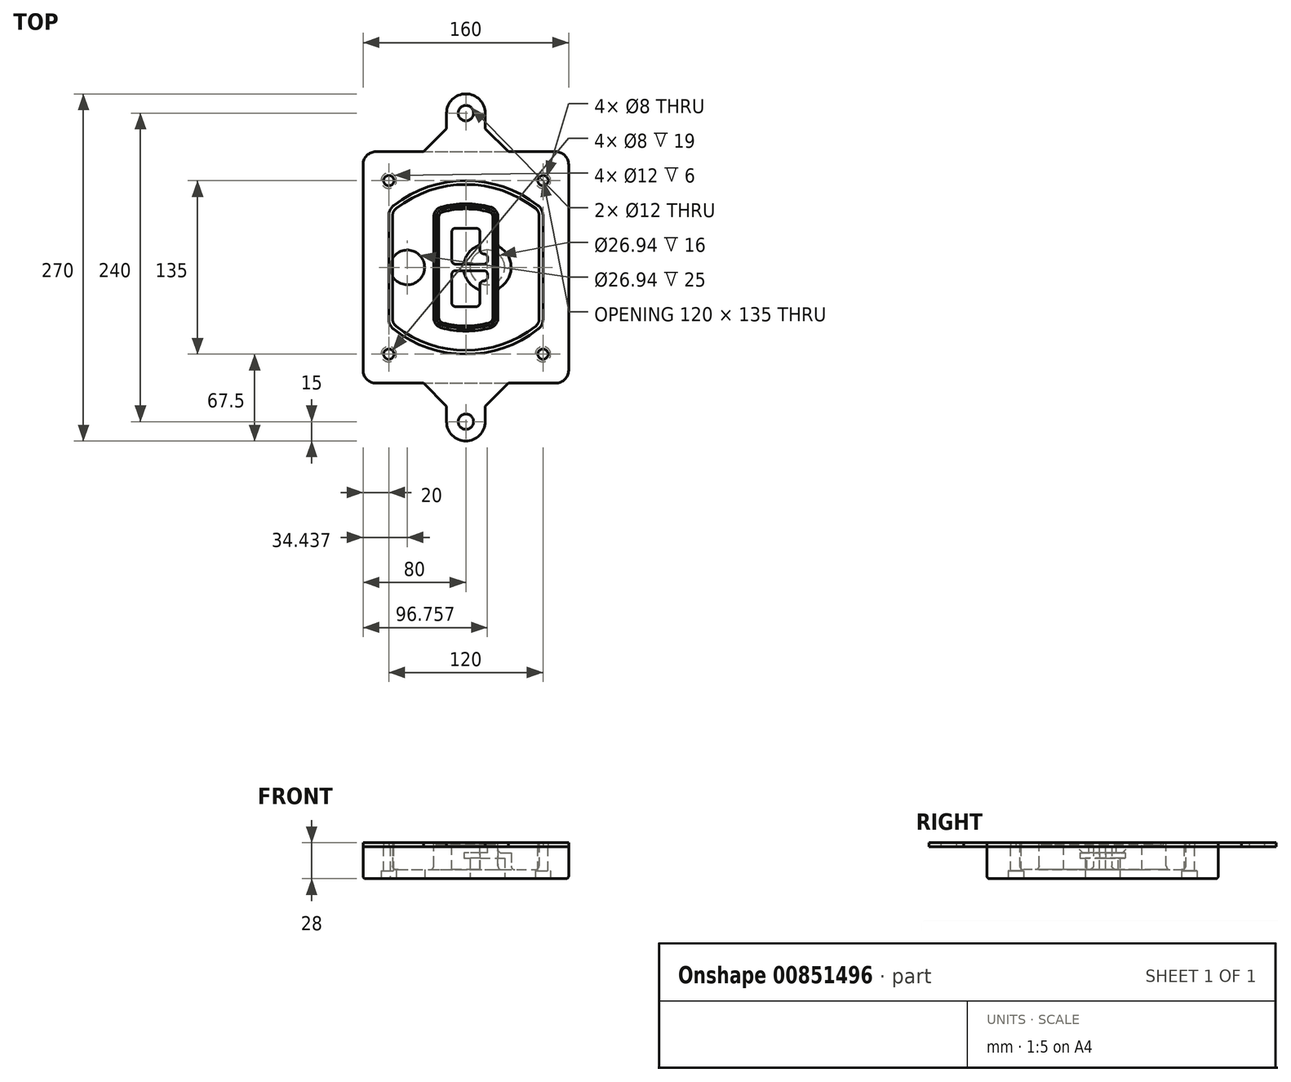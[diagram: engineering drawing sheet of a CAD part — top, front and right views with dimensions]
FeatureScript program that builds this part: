
annotation { "Feature Type Name" : "Feature", "Feature Type Description" : "" }
export const myFeature = defineFeature(function(context is Context, id is Id, definition is map)
    precondition{}
    {
        {
            var Q0;
            Q0=qCreatedBy(makeId("Top.planeOp"),FACE);
            var sketch = newSketch(context, id + "F0", { "sketchPlane" : qUnion([Q0])});
            skPoint(sketch, "E0.rect.middle", {"position": v(0, 0) * mm});
            skLineSegment(sketch, "E1.bottom", {"start": v(-70, -90) * mm, "end": v(70, -90) * mm});
            skLineSegment(sketch, "E1.top", {"start": v(-70, 90) * mm, "end": v(70, 90) * mm});
            skLineSegment(sketch, "E1.left", {"start": v(-80, -80) * mm, "end": v(-80, 80) * mm});
            skLineSegment(sketch, "E1.right", {"start": v(80, -80) * mm, "end": v(80, 80) * mm});
            skLineSegment(sketch, "E2", {"start": v(-80, 90) * mm, "end": v(80, -90) * mm, "construction": true});
            skLineSegment(sketch, "E3", {"start": v(80, 90) * mm, "end": v(-80, -90) * mm, "construction": true});
            skCircle(sketch, "E4", {"center": v(-60, 67.5) * mm, "radius": 4 * mm});
            skCircle(sketch, "E5", {"center": v(60, 67.5) * mm, "radius": 4 * mm});
            skCircle(sketch, "E6", {"center": v(60, -67.5) * mm, "radius": 4 * mm});
            skCircle(sketch, "E7", {"center": v(-60, -67.5) * mm, "radius": 4 * mm});
            skLineSegment(sketch, "E8", {"start": v(-60, 67.5) * mm, "end": v(60, 67.5) * mm, "construction": true});
            skLineSegment(sketch, "E9", {"start": v(60, 67.5) * mm, "end": v(60, -67.5) * mm, "construction": true});
            skLineSegment(sketch, "E10", {"start": v(60, -67.5) * mm, "end": v(-60, -67.5) * mm, "construction": true});
            skLineSegment(sketch, "E11", {"start": v(-60, -67.5) * mm, "end": v(-60, 67.5) * mm, "construction": true});
            skLineSegment(sketch, "E12", {"start": v(-60, 40.3) * mm, "end": v(-60, -40.3) * mm});
            skLineSegment(sketch, "E13", {"start": v(60, 40.3) * mm, "end": v(60, -40.3) * mm});
            skArc(sketch, "E14", {"start": v(56.15, 48.18) * mm, "mid": v(0, 67.5) * mm, "end": v(-56.15, 48.18) * mm});
            skArc(sketch, "E15", {"start": v(-56.15, -48.18) * mm, "mid": v(0, -67.5) * mm, "end": v(56.15, -48.18) * mm});
            skLineSegment(sketch, "E16", {"start": v(-60, 0) * mm, "end": v(60, 0) * mm, "construction": true});
            skPoint(sketch, "E17.visualSharp", {"position": v(-60, -45) * mm});
            skArc(sketch, "E17.filletArc", {"start": v(-60, -40.3) * mm, "mid": v(-58.99, -44.68) * mm, "end": v(-56.15, -48.18) * mm});
            skPoint(sketch, "E18.visualSharp", {"position": v(-60, 45) * mm});
            skArc(sketch, "E18.filletArc", {"start": v(-56.15, 48.18) * mm, "mid": v(-58.99, 44.68) * mm, "end": v(-60, 40.3) * mm});
            skPoint(sketch, "E19.visualSharp", {"position": v(60, 45) * mm});
            skArc(sketch, "E19.filletArc", {"start": v(60, 40.3) * mm, "mid": v(58.99, 44.68) * mm, "end": v(56.15, 48.18) * mm});
            skPoint(sketch, "E20.visualSharp", {"position": v(60, -45) * mm});
            skArc(sketch, "E20.filletArc", {"start": v(56.15, -48.18) * mm, "mid": v(58.99, -44.68) * mm, "end": v(60, -40.3) * mm});
            skPoint(sketch, "E21.visualSharp", {"position": v(-80, 90) * mm});
            skArc(sketch, "E21.filletArc", {"start": v(-70, 90) * mm, "mid": v(-77.07, 87.07) * mm, "end": v(-80, 80) * mm});
            skPoint(sketch, "E22.visualSharp", {"position": v(80, 90) * mm});
            skArc(sketch, "E22.filletArc", {"start": v(80, 80) * mm, "mid": v(77.07, 87.07) * mm, "end": v(70, 90) * mm});
            skPoint(sketch, "E23.visualSharp", {"position": v(80, -90) * mm});
            skArc(sketch, "E23.filletArc", {"start": v(70, -90) * mm, "mid": v(77.07, -87.07) * mm, "end": v(80, -80) * mm});
            skPoint(sketch, "E24.visualSharp", {"position": v(-80, -90) * mm});
            skArc(sketch, "E24.filletArc", {"start": v(-80, -80) * mm, "mid": v(-77.07, -87.07) * mm, "end": v(-70, -90) * mm});
            skArc(sketch, "E25.0", {"start": v(57, 40.3) * mm, "mid": v(56.3, 43.36) * mm, "end": v(54.3, 45.81) * mm});
            skLineSegment(sketch, "E25.1", {"start": v(57, 40.3) * mm, "end": v(57, -40.3) * mm});
            skArc(sketch, "E25.2", {"start": v(54.3, -45.81) * mm, "mid": v(56.3, -43.36) * mm, "end": v(57, -40.3) * mm});
            skArc(sketch, "E25.3", {"start": v(-54.3, -45.81) * mm, "mid": v(0, -64.5) * mm, "end": v(54.3, -45.81) * mm});
            skArc(sketch, "E25.4", {"start": v(-57, -40.3) * mm, "mid": v(-56.3, -43.36) * mm, "end": v(-54.3, -45.81) * mm});
            skArc(sketch, "E25.5", {"start": v(54.3, 45.81) * mm, "mid": v(0, 64.5) * mm, "end": v(-54.3, 45.81) * mm});
            skLineSegment(sketch, "E25.6", {"start": v(-57, 40.3) * mm, "end": v(-57, -40.3) * mm});
            skArc(sketch, "E25.7", {"start": v(-54.3, 45.81) * mm, "mid": v(-56.3, 43.36) * mm, "end": v(-57, 40.3) * mm});
            skArc(sketch, "E26.0", {"start": v(-58.62, 51.33) * mm, "mid": v(-62.58, 46.43) * mm, "end": v(-64, 40.3) * mm});
            skArc(sketch, "E26.1", {"start": v(58.62, 51.33) * mm, "mid": v(0, 71.5) * mm, "end": v(-58.62, 51.33) * mm});
            skArc(sketch, "E26.2", {"start": v(64, 40.3) * mm, "mid": v(62.58, 46.43) * mm, "end": v(58.62, 51.33) * mm});
            skLineSegment(sketch, "E26.3", {"start": v(64, 40.3) * mm, "end": v(64, -40.3) * mm});
            skArc(sketch, "E26.4", {"start": v(58.62, -51.33) * mm, "mid": v(62.58, -46.43) * mm, "end": v(64, -40.3) * mm});
            skLineSegment(sketch, "E26.5", {"start": v(-64, 40.3) * mm, "end": v(-64, -40.3) * mm});
            skArc(sketch, "E26.6", {"start": v(-58.62, -51.33) * mm, "mid": v(0, -71.5) * mm, "end": v(58.62, -51.33) * mm});
            skArc(sketch, "E26.7", {"start": v(-64, -40.3) * mm, "mid": v(-62.58, -46.43) * mm, "end": v(-58.62, -51.33) * mm});
            skSolve(sketch);
        }
        {
            var Q0;
            Q0=makeQuery(id+"F0.imprint","IMPRINT",FACE,{"disambiguationData":[TD([[makeQuery(id+"F0.imprint","IMPRINT",EDGE,{"derivedFrom":sQuery(id+"F0.wireOp",EDGE,"E1.bottom")}),1.0]])]});
            var Q1;
            Q1=makeQuery(id+"F0.imprint","IMPRINT",FACE,{"disambiguationData":[TD([[makeQuery(id+"F0.imprint","IMPRINT",EDGE,{"derivedFrom":sQuery(id+"F0.wireOp",EDGE,"E12")}),1.0]])]});
            var Q2;
            Q2=makeQuery(id+"F0.imprint","IMPRINT",FACE,{"disambiguationData":[TD([[makeQuery(id+"F0.imprint","IMPRINT",EDGE,{"derivedFrom":sQuery(id+"F0.wireOp",EDGE,"E25.0")}),1.0]])]});
            var Q3;
            Q3=makeQuery(id+"F0.imprint","IMPRINT",FACE,{"disambiguationData":[TD([[makeQuery(id+"F0.imprint","IMPRINT",EDGE,{"derivedFrom":sQuery(id+"F0.wireOp",EDGE,"E12")}),-1.0]])]});
            extrude(context, id + "F1", {"entities" : qUnion([Q0, Q1, Q2, Q3]), "oppositeDirection" : true, "depth" : 25 * mm});
        }
        {
            var Q0;
            Q0=makeQuery(id+"F0.imprint","IMPRINT",FACE,{"disambiguationData":[TD([[makeQuery(id+"F0.imprint","IMPRINT",EDGE,{"derivedFrom":sQuery(id+"F0.wireOp",EDGE,"E12")}),1.0]])]});
            extrude(context, id + "F2", {"entities" : qUnion([Q0]), "operationType" : NewBodyOperationType.ADD, "depth" : 3 * mm});
        }
        {
            var Q0;
            Q0=makeQuery(id+"F0.imprint","IMPRINT",FACE,{"disambiguationData":[TD([[makeQuery(id+"F0.imprint","IMPRINT",EDGE,{"derivedFrom":sQuery(id+"F0.wireOp",EDGE,"E25.0")}),1.0]])]});
            extrude(context, id + "F3", {"entities" : qUnion([Q0]), "operationType" : NewBodyOperationType.REMOVE, "oppositeDirection" : true, "depth" : 18 * mm});
        }
        {
            var Q0;
            Q0=makeQuery(id+"F2.opExtrude","CAP_FACE",FACE,{"disambiguationData":[OSD([sQuery(id+"F0.wireOp",EDGE,"E12"),sQuery(id+"F0.wireOp",EDGE,"E13"),sQuery(id+"F0.wireOp",EDGE,"E14"),sQuery(id+"F0.wireOp",EDGE,"E15"),sQuery(id+"F0.wireOp",EDGE,"E17.filletArc"),sQuery(id+"F0.wireOp",EDGE,"E18.filletArc"),sQuery(id+"F0.wireOp",EDGE,"E19.filletArc"),sQuery(id+"F0.wireOp",EDGE,"E20.filletArc"),sQuery(id+"F0.wireOp",EDGE,"E25.0"),sQuery(id+"F0.wireOp",EDGE,"E25.1"),sQuery(id+"F0.wireOp",EDGE,"E25.2"),sQuery(id+"F0.wireOp",EDGE,"E25.3"),sQuery(id+"F0.wireOp",EDGE,"E25.4"),sQuery(id+"F0.wireOp",EDGE,"E25.5"),sQuery(id+"F0.wireOp",EDGE,"E25.6"),sQuery(id+"F0.wireOp",EDGE,"E25.7")])],"isStart":false});
            var sketch = newSketch(context, id + "F4", { "sketchPlane" : qUnion([Q0])});
            skArc(sketch, "E27.0", {"start": v(-19.08, -46.97) * mm, "mid": v(0, -49.5) * mm, "end": v(19.08, -46.97) * mm});
            skArc(sketch, "E28.0", {"start": v(19.08, 46.97) * mm, "mid": v(0, 49.5) * mm, "end": v(-19.08, 46.97) * mm});
            skLineSegment(sketch, "E29", {"start": v(-25, 39.25) * mm, "end": v(-25, -39.25) * mm});
            skLineSegment(sketch, "E30", {"start": v(25, 39.25) * mm, "end": v(25, -39.25) * mm});
            skLineSegment(sketch, "E31", {"start": v(-25, 45.1) * mm, "end": v(25, 45.1) * mm, "construction": true});
            skLineSegment(sketch, "E32", {"start": v(-25, -45.1) * mm, "end": v(25, -45.1) * mm, "construction": true});
            skPoint(sketch, "E33.visualSharp", {"position": v(-25, 45.1) * mm});
            skArc(sketch, "E33.filletArc", {"start": v(-19.08, 46.97) * mm, "mid": v(-23.35, 44.11) * mm, "end": v(-25, 39.25) * mm});
            skPoint(sketch, "E34.visualSharp", {"position": v(25, 45.1) * mm});
            skArc(sketch, "E34.filletArc", {"start": v(25, 39.25) * mm, "mid": v(23.35, 44.11) * mm, "end": v(19.08, 46.97) * mm});
            skPoint(sketch, "E35.visualSharp", {"position": v(25, -45.1) * mm});
            skArc(sketch, "E35.filletArc", {"start": v(19.08, -46.97) * mm, "mid": v(23.35, -44.11) * mm, "end": v(25, -39.25) * mm});
            skPoint(sketch, "E36.visualSharp", {"position": v(-25, -45.1) * mm});
            skArc(sketch, "E36.filletArc", {"start": v(-25, -39.25) * mm, "mid": v(-23.35, -44.11) * mm, "end": v(-19.08, -46.97) * mm});
            skArc(sketch, "E37.0", {"start": v(54.3, 45.81) * mm, "mid": v(0, 64.5) * mm, "end": v(-54.3, 45.81) * mm});
            skArc(sketch, "E37.1", {"start": v(-54.3, 45.81) * mm, "mid": v(-56.3, 43.36) * mm, "end": v(-57, 40.3) * mm});
            skLineSegment(sketch, "E37.2", {"start": v(-57, 40.3) * mm, "end": v(-57, -40.3) * mm});
            skArc(sketch, "E37.3", {"start": v(-57, -40.3) * mm, "mid": v(-56.3, -43.36) * mm, "end": v(-54.3, -45.81) * mm});
            skArc(sketch, "E37.4", {"start": v(-54.3, -45.81) * mm, "mid": v(0, -64.5) * mm, "end": v(54.3, -45.81) * mm});
            skArc(sketch, "E37.5", {"start": v(54.3, -45.81) * mm, "mid": v(56.3, -43.36) * mm, "end": v(57, -40.3) * mm});
            skLineSegment(sketch, "E37.6", {"start": v(57, 40.3) * mm, "end": v(57, -40.3) * mm});
            skArc(sketch, "E37.7", {"start": v(57, 40.3) * mm, "mid": v(56.3, 43.36) * mm, "end": v(54.3, 45.81) * mm});
            skLineSegment(sketch, "E38.0", {"start": v(23, 39.25) * mm, "end": v(23, -39.25) * mm});
            skArc(sketch, "E38.1", {"start": v(18.56, -45.04) * mm, "mid": v(21.76, -42.9) * mm, "end": v(23, -39.25) * mm});
            skArc(sketch, "E38.2", {"start": v(-18.56, -45.04) * mm, "mid": v(0, -47.5) * mm, "end": v(18.56, -45.04) * mm});
            skArc(sketch, "E38.3", {"start": v(-23, -39.25) * mm, "mid": v(-21.76, -42.9) * mm, "end": v(-18.56, -45.04) * mm});
            skLineSegment(sketch, "E38.4", {"start": v(-23, 39.25) * mm, "end": v(-23, -39.25) * mm});
            skArc(sketch, "E38.5", {"start": v(23, 39.25) * mm, "mid": v(21.76, 42.9) * mm, "end": v(18.56, 45.04) * mm});
            skArc(sketch, "E38.6", {"start": v(-18.56, 45.04) * mm, "mid": v(-21.76, 42.9) * mm, "end": v(-23, 39.25) * mm});
            skArc(sketch, "E38.7", {"start": v(18.56, 45.04) * mm, "mid": v(0, 47.5) * mm, "end": v(-18.56, 45.04) * mm});
            skArc(sketch, "E39.0", {"start": v(21, 39.25) * mm, "mid": v(20.18, 41.68) * mm, "end": v(18.04, 43.1) * mm});
            skLineSegment(sketch, "E39.1", {"start": v(21, 39.25) * mm, "end": v(21, -39.25) * mm});
            skArc(sketch, "E39.2", {"start": v(18.04, -43.1) * mm, "mid": v(20.18, -41.68) * mm, "end": v(21, -39.25) * mm});
            skArc(sketch, "E39.3", {"start": v(-18.04, -43.1) * mm, "mid": v(0, -45.5) * mm, "end": v(18.04, -43.1) * mm});
            skArc(sketch, "E39.4", {"start": v(-21, -39.25) * mm, "mid": v(-20.18, -41.68) * mm, "end": v(-18.04, -43.1) * mm});
            skArc(sketch, "E39.5", {"start": v(18.04, 43.1) * mm, "mid": v(0, 45.5) * mm, "end": v(-18.04, 43.1) * mm});
            skLineSegment(sketch, "E39.6", {"start": v(-21, 39.25) * mm, "end": v(-21, -39.25) * mm});
            skArc(sketch, "E39.7", {"start": v(-18.04, 43.1) * mm, "mid": v(-20.18, 41.68) * mm, "end": v(-21, 39.25) * mm});
            skLineSegment(sketch, "E40", {"start": v(-25, 0) * mm, "end": v(25, 0) * mm, "construction": true});
            skLineSegment(sketch, "E41", {"start": v(-11, 5.5) * mm, "end": v(-11, 27.5) * mm});
            skLineSegment(sketch, "E42", {"start": v(-8, 30.5) * mm, "end": v(8, 30.5) * mm});
            skLineSegment(sketch, "E43", {"start": v(11, 27.5) * mm, "end": v(11, 13.5) * mm});
            skLineSegment(sketch, "E44", {"start": v(14, 10.5) * mm, "end": v(14, 10.5) * mm});
            skLineSegment(sketch, "E45", {"start": v(17, 7.5) * mm, "end": v(17, 5.5) * mm});
            skLineSegment(sketch, "E46", {"start": v(14, 2.5) * mm, "end": v(-8, 2.5) * mm});
            skPoint(sketch, "E47.visualSharp", {"position": v(-11, 30.5) * mm});
            skArc(sketch, "E47.filletArc", {"start": v(-8, 30.5) * mm, "mid": v(-10.12, 29.62) * mm, "end": v(-11, 27.5) * mm});
            skPoint(sketch, "E48.visualSharp", {"position": v(11, 30.5) * mm});
            skArc(sketch, "E48.filletArc", {"start": v(11, 27.5) * mm, "mid": v(10.12, 29.62) * mm, "end": v(8, 30.5) * mm});
            skPoint(sketch, "E49.visualSharp", {"position": v(11, 10.5) * mm});
            skArc(sketch, "E49.filletArc", {"start": v(11, 13.5) * mm, "mid": v(11.88, 11.38) * mm, "end": v(14, 10.5) * mm});
            skPoint(sketch, "E50.visualSharp", {"position": v(17, 10.5) * mm});
            skArc(sketch, "E50.filletArc", {"start": v(17, 7.5) * mm, "mid": v(16.12, 9.62) * mm, "end": v(14, 10.5) * mm});
            skPoint(sketch, "E51.visualSharp", {"position": v(17, 2.5) * mm});
            skArc(sketch, "E51.filletArc", {"start": v(14, 2.5) * mm, "mid": v(16.12, 3.38) * mm, "end": v(17, 5.5) * mm});
            skPoint(sketch, "E52.visualSharp", {"position": v(-11, 2.5) * mm});
            skArc(sketch, "E52.filletArc", {"start": v(-11, 5.5) * mm, "mid": v(-10.12, 3.38) * mm, "end": v(-8, 2.5) * mm});
            skLineSegment(sketch, "E53.0.MirrorCS", {"start": v(14, -2.5) * mm, "end": v(-8, -2.5) * mm});
            skArc(sketch, "E54.0.MirrorCS", {"start": v(-11, -5.5) * mm, "mid": v(-10.12, -3.38) * mm, "end": v(-8, -2.5) * mm});
            skLineSegment(sketch, "E55.0.MirrorCS", {"start": v(-11, -5.5) * mm, "end": v(-11, -27.5) * mm});
            skArc(sketch, "E56.0.MirrorCS", {"start": v(-8, -30.5) * mm, "mid": v(-10.12, -29.62) * mm, "end": v(-11, -27.5) * mm});
            skLineSegment(sketch, "E57.0.MirrorCS", {"start": v(-8, -30.5) * mm, "end": v(8, -30.5) * mm});
            skArc(sketch, "E58.0.MirrorCS", {"start": v(11, -27.5) * mm, "mid": v(10.12, -29.62) * mm, "end": v(8, -30.5) * mm});
            skLineSegment(sketch, "E59.0.MirrorCS", {"start": v(11, -27.5) * mm, "end": v(11, -13.5) * mm});
            skArc(sketch, "E60.0.MirrorCS", {"start": v(11, -13.5) * mm, "mid": v(11.88, -11.38) * mm, "end": v(14, -10.5) * mm});
            skArc(sketch, "E61.0.MirrorCS", {"start": v(17, -7.5) * mm, "mid": v(16.12, -9.62) * mm, "end": v(14, -10.5) * mm});
            skLineSegment(sketch, "E62.0.MirrorCS", {"start": v(17, -7.5) * mm, "end": v(17, -5.5) * mm});
            skArc(sketch, "E63.0.MirrorCS", {"start": v(14, -2.5) * mm, "mid": v(16.12, -3.38) * mm, "end": v(17, -5.5) * mm});
            skSolve(sketch);
        }
        {
            var Q0;
            Q0=makeQuery(id+"F4.imprint","IMPRINT",FACE,{"disambiguationData":[TD([[makeQuery(id+"F4.imprint","IMPRINT",EDGE,{"derivedFrom":sQuery(id+"F4.wireOp",EDGE,"E27.0")}),1.0]])]});
            var Q1;
            Q1=makeQuery(id+"F4.imprint","IMPRINT",FACE,{"disambiguationData":[TD([[makeQuery(id+"F4.imprint","IMPRINT",EDGE,{"derivedFrom":sQuery(id+"F4.wireOp",EDGE,"E38.0")}),-1.0]])]});
            var Q2;
            Q2=makeQuery(id+"F4.imprint","IMPRINT",FACE,{"disambiguationData":[TD([[makeQuery(id+"F4.imprint","IMPRINT",EDGE,{"derivedFrom":sQuery(id+"F4.wireOp",EDGE,"E39.0")}),1.0]])]});
            extrude(context, id + "F5", {"entities" : qUnion([Q0, Q1, Q2]), "operationType" : NewBodyOperationType.ADD, "endBound" : BoundingType.UP_TO_NEXT, "oppositeDirection" : true, "depth" : 25 * mm});
        }
        {
            var Q0;
            Q0=makeQuery(id+"F4.imprint","IMPRINT",FACE,{"disambiguationData":[TD([[makeQuery(id+"F4.imprint","IMPRINT",EDGE,{"derivedFrom":sQuery(id+"F4.wireOp",EDGE,"E38.0")}),-1.0]])]});
            extrude(context, id + "F6", {"entities" : qUnion([Q0]), "operationType" : NewBodyOperationType.REMOVE, "oppositeDirection" : true, "depth" : 2 * mm});
        }
        {
            var Q0;
            Q0=makeQuery(id+"F1.opExtrude","CAP_FACE",FACE,{"disambiguationData":[OSD([sQuery(id+"F0.wireOp",EDGE,"E1.bottom"),sQuery(id+"F0.wireOp",EDGE,"E1.top"),sQuery(id+"F0.wireOp",EDGE,"E1.left"),sQuery(id+"F0.wireOp",EDGE,"E1.right"),sQuery(id+"F0.wireOp",EDGE,"E4"),sQuery(id+"F0.wireOp",EDGE,"E5"),sQuery(id+"F0.wireOp",EDGE,"E6"),sQuery(id+"F0.wireOp",EDGE,"E7"),sQuery(id+"F0.wireOp",EDGE,"E21.filletArc"),sQuery(id+"F0.wireOp",EDGE,"E22.filletArc"),sQuery(id+"F0.wireOp",EDGE,"E23.filletArc"),sQuery(id+"F0.wireOp",EDGE,"E24.filletArc")])],"isStart":false});
            var sketch = newSketch(context, id + "F7", { "sketchPlane" : qUnion([Q0])});
            skCircle(sketch, "E64", {"center": v(16.76, 0) * mm, "radius": 13.47 * mm});
            skCircle(sketch, "E65", {"center": v(-45.56, 0) * mm, "radius": 13.47 * mm});
            skLineSegment(sketch, "E66", {"start": v(80, 0) * mm, "end": v(-80, 0) * mm});
            skCircle(sketch, "E67", {"center": v(16.76, 0) * mm, "radius": 18.47 * mm});
            skCircle(sketch, "E68", {"center": v(60, -67.5) * mm, "radius": 6 * mm});
            skCircle(sketch, "E69", {"center": v(-60, -67.5) * mm, "radius": 6 * mm});
            skCircle(sketch, "E70", {"center": v(-60, 67.5) * mm, "radius": 6 * mm});
            skCircle(sketch, "E71", {"center": v(60, 67.5) * mm, "radius": 6 * mm});
            skSolve(sketch);
        }
        {
            var Q0;
            {var subQ1=sQuery(id+"F7.wireOp",EDGE,"E66");var subQ4=sQuery(id+"F7.wireOp",EDGE,"E64");var subQ6=makeQuery(id+"F7.imprint","INTERSECT",VERTEX,{"disambiguationData":[OD(0.0)],"derivedFrom":[subQ4,subQ1]});Q0=makeQuery(id+"F7.imprint","IMPRINT",FACE,{"disambiguationData":[TD([[makeQuery(id+"F7.imprint","IMPRINT",EDGE,{"disambiguationData":[TD([[subQ6,-1.0]])],"derivedFrom":subQ4}),-1.0]])]});}
            var Q1;
            {var subQ0=sQuery(id+"F7.wireOp",EDGE,"E66");var subQ1=sQuery(id+"F7.wireOp",EDGE,"E64");var subQ3=makeQuery(id+"F7.imprint","INTERSECT",VERTEX,{"disambiguationData":[OD(0.0)],"derivedFrom":[subQ1,subQ0]});Q1=makeQuery(id+"F7.imprint","IMPRINT",FACE,{"disambiguationData":[TD([[makeQuery(id+"F7.imprint","IMPRINT",EDGE,{"disambiguationData":[TD([[subQ3,-1.0]])],"derivedFrom":subQ1}),1.0]])]});}
            var Q2;
            {var subQ0=sQuery(id+"F7.wireOp",EDGE,"E66");var subQ1=sQuery(id+"F7.wireOp",EDGE,"E64");var subQ3=makeQuery(id+"F7.imprint","INTERSECT",VERTEX,{"disambiguationData":[OD(0.0)],"derivedFrom":[subQ1,subQ0]});Q2=makeQuery(id+"F7.imprint","IMPRINT",FACE,{"disambiguationData":[TD([[makeQuery(id+"F7.imprint","IMPRINT",EDGE,{"disambiguationData":[TD([[subQ3,1.0]])],"derivedFrom":subQ1}),1.0]])]});}
            var Q3;
            {var subQ1=sQuery(id+"F7.wireOp",EDGE,"E66");var subQ4=sQuery(id+"F7.wireOp",EDGE,"E64");var subQ6=makeQuery(id+"F7.imprint","INTERSECT",VERTEX,{"disambiguationData":[OD(0.0)],"derivedFrom":[subQ4,subQ1]});Q3=makeQuery(id+"F7.imprint","IMPRINT",FACE,{"disambiguationData":[TD([[makeQuery(id+"F7.imprint","IMPRINT",EDGE,{"disambiguationData":[TD([[subQ6,1.0]])],"derivedFrom":subQ4}),-1.0]])]});}
            extrude(context, id + "F8", {"entities" : qUnion([Q0, Q1, Q2, Q3]), "operationType" : NewBodyOperationType.ADD, "oppositeDirection" : true, "depth" : 20 * mm});
        }
        {
            var Q0;
            {var subQ0=sQuery(id+"F7.wireOp",EDGE,"E66");var subQ1=sQuery(id+"F7.wireOp",EDGE,"E64");var subQ3=makeQuery(id+"F7.imprint","INTERSECT",VERTEX,{"disambiguationData":[OD(0.0)],"derivedFrom":[subQ1,subQ0]});Q0=makeQuery(id+"F7.imprint","IMPRINT",FACE,{"disambiguationData":[TD([[makeQuery(id+"F7.imprint","IMPRINT",EDGE,{"disambiguationData":[TD([[subQ3,-1.0]])],"derivedFrom":subQ1}),1.0]])]});}
            var Q1;
            {var subQ0=sQuery(id+"F7.wireOp",EDGE,"E66");var subQ1=sQuery(id+"F7.wireOp",EDGE,"E64");var subQ3=makeQuery(id+"F7.imprint","INTERSECT",VERTEX,{"disambiguationData":[OD(0.0)],"derivedFrom":[subQ1,subQ0]});Q1=makeQuery(id+"F7.imprint","IMPRINT",FACE,{"disambiguationData":[TD([[makeQuery(id+"F7.imprint","IMPRINT",EDGE,{"disambiguationData":[TD([[subQ3,1.0]])],"derivedFrom":subQ1}),1.0]])]});}
            extrude(context, id + "F9", {"entities" : qUnion([Q0, Q1]), "operationType" : NewBodyOperationType.REMOVE, "oppositeDirection" : true, "depth" : 16 * mm});
        }
        {
            var Q0;
            {var subQ0=sQuery(id+"F7.wireOp",EDGE,"E66");var subQ1=sQuery(id+"F7.wireOp",EDGE,"E65");var subQ3=makeQuery(id+"F7.imprint","INTERSECT",VERTEX,{"disambiguationData":[OD(0.0)],"derivedFrom":[subQ1,subQ0]});Q0=makeQuery(id+"F7.imprint","IMPRINT",FACE,{"disambiguationData":[TD([[makeQuery(id+"F7.imprint","IMPRINT",EDGE,{"disambiguationData":[TD([[subQ3,-1.0]])],"derivedFrom":subQ1}),1.0]])]});}
            var Q1;
            {var subQ0=sQuery(id+"F7.wireOp",EDGE,"E66");var subQ1=sQuery(id+"F7.wireOp",EDGE,"E65");var subQ3=makeQuery(id+"F7.imprint","INTERSECT",VERTEX,{"disambiguationData":[OD(0.0)],"derivedFrom":[subQ1,subQ0]});Q1=makeQuery(id+"F7.imprint","IMPRINT",FACE,{"disambiguationData":[TD([[makeQuery(id+"F7.imprint","IMPRINT",EDGE,{"disambiguationData":[TD([[subQ3,1.0]])],"derivedFrom":subQ1}),1.0]])]});}
            extrude(context, id + "F10", {"entities" : qUnion([Q0, Q1]), "operationType" : NewBodyOperationType.REMOVE, "oppositeDirection" : true, "depth" : 25 * mm});
        }
        {
            var Q0;
            Q0=makeQuery(id+"F7.imprint","IMPRINT",FACE,{"disambiguationData":[TD([[makeQuery(id+"F7.imprint","IMPRINT",EDGE,{"derivedFrom":sQuery(id+"F7.wireOp",EDGE,"E68")}),1.0]])]});
            var Q1;
            Q1=makeQuery(id+"F7.imprint","IMPRINT",FACE,{"disambiguationData":[TD([[makeQuery(id+"F7.imprint","IMPRINT",EDGE,{"derivedFrom":makeQuery(id+"F1.opExtrude","CAP_EDGE",EDGE,{"disambiguationData":[OSD([sQuery(id+"F0.wireOp",EDGE,"E5")])],"isStart":false})}),-1.0]])]});
            var Q2;
            Q2=makeQuery(id+"F7.imprint","IMPRINT",FACE,{"disambiguationData":[TD([[makeQuery(id+"F7.imprint","IMPRINT",EDGE,{"derivedFrom":sQuery(id+"F7.wireOp",EDGE,"E69")}),1.0]])]});
            var Q3;
            Q3=makeQuery(id+"F7.imprint","IMPRINT",FACE,{"disambiguationData":[TD([[makeQuery(id+"F7.imprint","IMPRINT",EDGE,{"derivedFrom":makeQuery(id+"F1.opExtrude","CAP_EDGE",EDGE,{"disambiguationData":[OSD([sQuery(id+"F0.wireOp",EDGE,"E4")])],"isStart":false})}),-1.0]])]});
            var Q4;
            Q4=makeQuery(id+"F7.imprint","IMPRINT",FACE,{"disambiguationData":[TD([[makeQuery(id+"F7.imprint","IMPRINT",EDGE,{"derivedFrom":sQuery(id+"F7.wireOp",EDGE,"E70")}),1.0]])]});
            var Q5;
            Q5=makeQuery(id+"F7.imprint","IMPRINT",FACE,{"disambiguationData":[TD([[makeQuery(id+"F7.imprint","IMPRINT",EDGE,{"derivedFrom":makeQuery(id+"F1.opExtrude","CAP_EDGE",EDGE,{"disambiguationData":[OSD([sQuery(id+"F0.wireOp",EDGE,"E7")])],"isStart":false})}),-1.0]])]});
            var Q6;
            Q6=makeQuery(id+"F7.imprint","IMPRINT",FACE,{"disambiguationData":[TD([[makeQuery(id+"F7.imprint","IMPRINT",EDGE,{"derivedFrom":sQuery(id+"F7.wireOp",EDGE,"E71")}),1.0]])]});
            var Q7;
            Q7=makeQuery(id+"F7.imprint","IMPRINT",FACE,{"disambiguationData":[TD([[makeQuery(id+"F7.imprint","IMPRINT",EDGE,{"derivedFrom":makeQuery(id+"F1.opExtrude","CAP_EDGE",EDGE,{"disambiguationData":[OSD([sQuery(id+"F0.wireOp",EDGE,"E6")])],"isStart":false})}),-1.0]])]});
            extrude(context, id + "F11", {"entities" : qUnion([Q0, Q1, Q2, Q3, Q4, Q5, Q6, Q7]), "operationType" : NewBodyOperationType.REMOVE, "oppositeDirection" : true, "depth" : 6 * mm});
        }
        {
            var Q0;
            Q0=makeQuery(id+"F9.boolean.opBoolean","COPY",FACE,{"derivedFrom":makeQuery(id+"F9.opExtrude","CAP_FACE",FACE,{"disambiguationData":[OSD([sQuery(id+"F7.wireOp",EDGE,"E64")])],"isStart":false})});
            var sketch = newSketch(context, id + "F12", { "sketchPlane" : qUnion([Q0])});
            skArc(sketch, "E72.0", {"start": v(11, 17.55) * mm, "mid": v(2.57, 11.82) * mm, "end": v(-1.54, 2.5) * mm});
            skArc(sketch, "E72.1", {"start": v(-1.54, -2.5) * mm, "mid": v(2.57, -11.82) * mm, "end": v(11, -17.55) * mm});
            skLineSegment(sketch, "E73", {"start": v(-1.54, -2.5) * mm, "end": v(14, -2.5) * mm});
            skLineSegment(sketch, "E74.0", {"start": v(14, 2.5) * mm, "end": v(-1.54, 2.5) * mm});
            skArc(sketch, "E74.1", {"start": v(14, 2.5) * mm, "mid": v(16.12, 3.38) * mm, "end": v(17, 5.5) * mm});
            skLineSegment(sketch, "E74.2", {"start": v(17, 7.5) * mm, "end": v(17, 5.5) * mm});
            skArc(sketch, "E74.3", {"start": v(17, 7.5) * mm, "mid": v(16.12, 9.62) * mm, "end": v(14, 10.5) * mm});
            skArc(sketch, "E74.4", {"start": v(11, 13.5) * mm, "mid": v(11.88, 11.38) * mm, "end": v(14, 10.5) * mm});
            skLineSegment(sketch, "E74.5", {"start": v(11, 17.55) * mm, "end": v(11, 13.5) * mm});
            skLineSegment(sketch, "E74.7", {"start": v(14, -2.5) * mm, "end": v(-1.54, -2.5) * mm});
            skArc(sketch, "E74.8", {"start": v(14, -2.5) * mm, "mid": v(16.12, -3.38) * mm, "end": v(17, -5.5) * mm});
            skLineSegment(sketch, "E74.9", {"start": v(17, -7.5) * mm, "end": v(17, -5.5) * mm});
            skArc(sketch, "E74.10", {"start": v(17, -7.5) * mm, "mid": v(16.12, -9.62) * mm, "end": v(14, -10.5) * mm});
            skArc(sketch, "E74.11", {"start": v(11, -13.5) * mm, "mid": v(11.88, -11.38) * mm, "end": v(14, -10.5) * mm});
            skLineSegment(sketch, "E74.12", {"start": v(11, -17.55) * mm, "end": v(11, -13.5) * mm});
            skPoint(sketch, "E75.orphan", {"position": v(11, -27.5) * mm});
            skPoint(sketch, "E76.orphan", {"position": v(-8, -2.5) * mm});
            skPoint(sketch, "E77.orphan", {"position": v(-8, 2.5) * mm});
            skPoint(sketch, "E78.orphan", {"position": v(11, 27.5) * mm});
            skSolve(sketch);
        }
        {
            var Q0;
            {var subQ7=sQuery(id+"F12.wireOp",EDGE,"E72.0");var subQ14=sQuery(id+"F12.wireOp",EDGE,"E72.1");var subQ16=sQuery(id+"F12.wireOp",EDGE,"E74.1");var subQ18=sQuery(id+"F12.wireOp",EDGE,"E74.8");Q0=qUnion([makeQuery(id+"F12.imprint","IMPRINT",FACE,{"disambiguationData":[TD([[makeQuery(id+"F12.imprint","IMPRINT",EDGE,{"derivedFrom":subQ7}),1.0]])]}),makeQuery(id+"F12.imprint","IMPRINT",FACE,{"disambiguationData":[TD([[makeQuery(id+"F12.imprint","IMPRINT",EDGE,{"derivedFrom":subQ14}),1.0]])]}),makeQuery(id+"F12.imprint","IMPRINT",FACE,{"disambiguationData":[TD([[makeQuery(id+"F12.imprint","IMPRINT",EDGE,{"derivedFrom":subQ16}),1.0]])]}),makeQuery(id+"F12.imprint","IMPRINT",FACE,{"disambiguationData":[TD([[makeQuery(id+"F12.imprint","IMPRINT",EDGE,{"derivedFrom":subQ18}),-1.0]])]})]);}
            var Q1;
            Q1=makeQuery(id+"F5.boolean.opBoolean","SPLIT",FACE,{"disambiguationData":[TD([makeQuery(id+"F5.opExtrude","SWEPT_FACE",FACE,{"disambiguationData":[OSD([sQuery(id+"F4.wireOp",EDGE,"E41")])]})])],"derivedFrom":makeQuery(id+"F3.boolean.opBoolean","COPY",FACE,{"derivedFrom":makeQuery(id+"F3.opExtrude","CAP_FACE",FACE,{"disambiguationData":[OSD([sQuery(id+"F0.wireOp",EDGE,"E25.0"),sQuery(id+"F0.wireOp",EDGE,"E25.1"),sQuery(id+"F0.wireOp",EDGE,"E25.2"),sQuery(id+"F0.wireOp",EDGE,"E25.3"),sQuery(id+"F0.wireOp",EDGE,"E25.4"),sQuery(id+"F0.wireOp",EDGE,"E25.5"),sQuery(id+"F0.wireOp",EDGE,"E25.6"),sQuery(id+"F0.wireOp",EDGE,"E25.7")])],"isStart":false})})});
            extrude(context, id + "F13", {"entities" : qUnion([Q0]), "operationType" : NewBodyOperationType.REMOVE, "endBound" : BoundingType.UP_TO_SURFACE, "endBoundEntityFace" : qUnion([Q1]), "depth" : 25 * mm});
        }
        {
            var Q0;
            Q0=makeQuery(id+"F3.boolean.opBoolean","COPY",EDGE,{"derivedFrom":makeQuery(id+"F3.opExtrude","CAP_EDGE",EDGE,{"disambiguationData":[OSD([sQuery(id+"F0.wireOp",EDGE,"E25.6")])],"isStart":false})});
            var Q1;
            Q1=makeQuery(id+"F8.boolean.opBoolean","INTERSECT",EDGE,{"derivedFrom":[makeQuery(id+"F5.opExtrude","SWEPT_FACE",FACE,{"disambiguationData":[OSD([sQuery(id+"F4.wireOp",EDGE,"E30")])]}),makeQuery(id+"F8.opExtrude","CAP_FACE",FACE,{"disambiguationData":[OSD([sQuery(id+"F7.wireOp",EDGE,"E67")])],"isStart":false})]});
            var Q2;
            Q2=makeQuery(id+"F8.boolean.opBoolean","INTERSECT",EDGE,{"disambiguationData":[OD(1.0)],"derivedFrom":[makeQuery(id+"F5.opExtrude","SWEPT_FACE",FACE,{"disambiguationData":[OSD([sQuery(id+"F4.wireOp",EDGE,"E30")])]}),makeQuery(id+"F8.opExtrude","SWEPT_FACE",FACE,{"disambiguationData":[OSD([sQuery(id+"F7.wireOp",EDGE,"E67")])]})]});
            var Q3;
            {var subQ0=sQuery(id+"F4.wireOp",EDGE,"E30");Q3=makeQuery(id+"F8.boolean.opBoolean","SPLIT",EDGE,{"disambiguationData":[TD([makeQuery(id+"F5.opExtrude","SWEPT_FACE",FACE,{"disambiguationData":[OSD([sQuery(id+"F4.wireOp",EDGE,"E35.filletArc")])]})])],"derivedFrom":makeQuery(id+"F5.opExtrude","CAP_EDGE",EDGE,{"disambiguationData":[OSD([subQ0])],"isStart":false})});}
            var Q4;
            {var subQ0=sQuery(id+"F0.wireOp",EDGE,"E25.7");var subQ1=sQuery(id+"F0.wireOp",EDGE,"E25.1");var subQ2=sQuery(id+"F0.wireOp",EDGE,"E25.6");var subQ3=sQuery(id+"F0.wireOp",EDGE,"E25.5");var subQ4=sQuery(id+"F0.wireOp",EDGE,"E25.4");var subQ5=sQuery(id+"F0.wireOp",EDGE,"E25.0");var subQ6=sQuery(id+"F0.wireOp",EDGE,"E25.2");var subQ7=sQuery(id+"F0.wireOp",EDGE,"E25.3");Q4=makeQuery(id+"F8.boolean.opBoolean","INTERSECT",EDGE,{"derivedFrom":[makeQuery(id+"F5.boolean.opBoolean","SPLIT",FACE,{"disambiguationData":[TD([makeQuery(id+"F2.opExtrude","SWEPT_FACE",FACE,{"disambiguationData":[OSD([subQ5])]})])],"derivedFrom":makeQuery(id+"F3.boolean.opBoolean","COPY",FACE,{"derivedFrom":makeQuery(id+"F3.opExtrude","CAP_FACE",FACE,{"disambiguationData":[OSD([subQ5,subQ1,subQ6,subQ7,subQ4,subQ3,subQ2,subQ0])],"isStart":false})})}),makeQuery(id+"F8.opExtrude","SWEPT_FACE",FACE,{"disambiguationData":[OSD([sQuery(id+"F7.wireOp",EDGE,"E67")])]})]});}
            var Q5;
            Q5=makeQuery(id+"F8.boolean.opBoolean","INTERSECT",EDGE,{"disambiguationData":[OD(0.0)],"derivedFrom":[makeQuery(id+"F5.opExtrude","SWEPT_FACE",FACE,{"disambiguationData":[OSD([sQuery(id+"F4.wireOp",EDGE,"E30")])]}),makeQuery(id+"F8.opExtrude","SWEPT_FACE",FACE,{"disambiguationData":[OSD([sQuery(id+"F7.wireOp",EDGE,"E67")])]})]});
            fillet(context, id + "F14", {"entities" : qUnion([Q0, Q1, Q2, Q3, Q4, Q5]), "radius" : 3 * mm, "tangentPropagation" : true, "allowEdgeOverflow" : false});
        }
        {
            var Q0;
            Q0=makeQuery(id+"F1.opExtrude","CAP_EDGE",EDGE,{"disambiguationData":[OSD([sQuery(id+"F0.wireOp",EDGE,"E1.bottom")])],"isStart":false});
            fillet(context, id + "F15", {"entities" : qUnion([Q0]), "radius" : 2 * mm, "tangentPropagation" : true, "allowEdgeOverflow" : false});
        }
        {
            var Q0;
            {var subQ0=sQuery(id+"F0.wireOp",EDGE,"E21.filletArc");var subQ1=sQuery(id+"F0.wireOp",EDGE,"E7");var subQ2=sQuery(id+"F0.wireOp",EDGE,"E6");var subQ3=sQuery(id+"F0.wireOp",EDGE,"E5");var subQ4=sQuery(id+"F0.wireOp",EDGE,"E4");var subQ5=sQuery(id+"F0.wireOp",EDGE,"E22.filletArc");var subQ6=sQuery(id+"F0.wireOp",EDGE,"E1.bottom");var subQ7=sQuery(id+"F0.wireOp",EDGE,"E1.right");var subQ8=sQuery(id+"F0.wireOp",EDGE,"E1.top");var subQ9=sQuery(id+"F0.wireOp",EDGE,"E1.left");var subQ10=sQuery(id+"F0.wireOp",EDGE,"E23.filletArc");var subQ11=sQuery(id+"F0.wireOp",EDGE,"E24.filletArc");Q0=makeQuery(id+"F2.boolean.opBoolean","SPLIT",FACE,{"disambiguationData":[TD([makeQuery(id+"F1.opExtrude","SWEPT_FACE",FACE,{"disambiguationData":[OSD([subQ6])]})])],"derivedFrom":makeQuery(id+"F1.opExtrude","CAP_FACE",FACE,{"disambiguationData":[OSD([subQ6,subQ8,subQ9,subQ7,subQ4,subQ3,subQ2,subQ1,subQ0,subQ5,subQ10,subQ11])],"isStart":true})});}
            var sketch = newSketch(context, id + "F16", { "sketchPlane" : qUnion([Q0])});
            skLineSegment(sketch, "E79", {"start": v(-33, 90) * mm, "end": v(-15, 108) * mm});
            skLineSegment(sketch, "E80", {"start": v(-15, 108) * mm, "end": v(-15, 120) * mm});
            skLineSegment(sketch, "E81", {"start": v(33, 90) * mm, "end": v(15, 108) * mm});
            skLineSegment(sketch, "E82", {"start": v(15, 108) * mm, "end": v(15, 120) * mm});
            skLineSegment(sketch, "E83", {"start": v(0, 90) * mm, "end": v(0, 120) * mm, "construction": true});
            skCircle(sketch, "E84", {"center": v(0, 120) * mm, "radius": 6 * mm});
            skArc(sketch, "E85", {"start": v(15, 120) * mm, "mid": v(0, 135) * mm, "end": v(-15, 120) * mm});
            skLineSegment(sketch, "E86", {"start": v(-80, 0) * mm, "end": v(80, 0) * mm, "construction": true});
            skLineSegment(sketch, "E87.MirrorCS", {"start": v(33, -90) * mm, "end": v(15, -108) * mm});
            skCircle(sketch, "E88.MirrorC", {"center": v(0, -120) * mm, "radius": 6 * mm});
            skLineSegment(sketch, "E89.MirrorCS", {"start": v(-15, -108) * mm, "end": v(-15, -120) * mm});
            skArc(sketch, "E90.MirrorCS", {"start": v(15, -120) * mm, "mid": v(0, -135) * mm, "end": v(-15, -120) * mm});
            skLineSegment(sketch, "E91.MirrorCS", {"start": v(-33, -90) * mm, "end": v(-15, -108) * mm});
            skLineSegment(sketch, "E92.MirrorCS", {"start": v(0, -90) * mm, "end": v(0, -120) * mm, "construction": true});
            skLineSegment(sketch, "E93.MirrorCS", {"start": v(15, -108) * mm, "end": v(15, -120) * mm});
            skSolve(sketch);
        }
        {
            var Q0;
            {var subQ0=sQuery(id+"F16.wireOp",EDGE,"E87.MirrorCS");Q0=makeQuery(id+"F16.imprint","IMPRINT",FACE,{"disambiguationData":[TD([[makeQuery(id+"F16.imprint","IMPRINT",EDGE,{"derivedFrom":subQ0}),-1.0]])]});}
            var Q1;
            Q1=makeQuery(id+"F16.imprint","IMPRINT",FACE,{"disambiguationData":[TD([[makeQuery(id+"F16.imprint","IMPRINT",EDGE,{"derivedFrom":makeQuery(id+"F1.opExtrude","CAP_EDGE",EDGE,{"disambiguationData":[OSD([sQuery(id+"F0.wireOp",EDGE,"E1.left")])],"isStart":true})}),-1.0]])]});
            var Q2;
            {var subQ1=sQuery(id+"F16.wireOp",EDGE,"E79");Q2=makeQuery(id+"F16.imprint","IMPRINT",FACE,{"disambiguationData":[TD([[makeQuery(id+"F16.imprint","IMPRINT",EDGE,{"derivedFrom":subQ1}),-1.0]])]});}
            var Q3;
            Q3=makeQuery(id+"F2.opExtrude","CAP_FACE",FACE,{"disambiguationData":[OSD([sQuery(id+"F0.wireOp",EDGE,"E12"),sQuery(id+"F0.wireOp",EDGE,"E13"),sQuery(id+"F0.wireOp",EDGE,"E14"),sQuery(id+"F0.wireOp",EDGE,"E15"),sQuery(id+"F0.wireOp",EDGE,"E17.filletArc"),sQuery(id+"F0.wireOp",EDGE,"E18.filletArc"),sQuery(id+"F0.wireOp",EDGE,"E19.filletArc"),sQuery(id+"F0.wireOp",EDGE,"E20.filletArc"),sQuery(id+"F0.wireOp",EDGE,"E25.0"),sQuery(id+"F0.wireOp",EDGE,"E25.1"),sQuery(id+"F0.wireOp",EDGE,"E25.2"),sQuery(id+"F0.wireOp",EDGE,"E25.3"),sQuery(id+"F0.wireOp",EDGE,"E25.4"),sQuery(id+"F0.wireOp",EDGE,"E25.5"),sQuery(id+"F0.wireOp",EDGE,"E25.6"),sQuery(id+"F0.wireOp",EDGE,"E25.7")])],"isStart":false});
            extrude(context, id + "F17", {"entities" : qUnion([Q0, Q1, Q2]), "endBound" : BoundingType.UP_TO_SURFACE, "depth" : 25 * mm, "endBoundEntityFace" : qUnion([Q3]), "offsetDistance" : 25 * mm});
        }
    });
